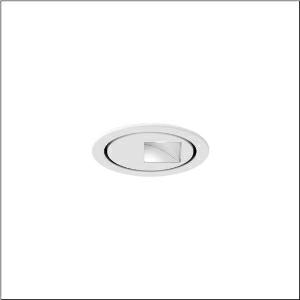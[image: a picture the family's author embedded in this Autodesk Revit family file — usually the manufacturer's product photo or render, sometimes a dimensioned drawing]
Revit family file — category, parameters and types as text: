
# Revit family: lunis_11_micro_round_51dj11b71wg21
name_source: partatom
category: Lighting Fixtures
units: mm (PartAtom-declared; Revit-internal decimal feet)

## family parameters
Cut with Voids When Loaded = No
Host = Face
Light Source = No
Part Type = Normal
Room Calculation Point = No
Round Connector Dimension = Use Diameter
Shared = No

## types (1)
- Lunis 11 micro round (1 x LED 4000K / CRI = 80 (unbekannt), 1400 lm, 4000K)
    Apparent Load = 20 VA
    CIE Flux Codes = 42 75 96 100 100
    Color Rendering = 80
    Color Temperature = 4000K
    Default Elevation = 1800 mm
    Description = Lunis 11 micro round, downlight, light control with wallwasher, of highly reflective aluminium, highly specular, light emission: direct distribution, LED rated luminous flux: 1.400lm, light colour: 840, with terminal, 3-pole, mains connection: 220..230V, AC, 50/60Hz, LED module, of aluminium, highly specular, white, diameter: 114mm, clamping range: 1..40mm, recessing ring, of plastic, traffic white (RAL 9016), protection rating (complete): IP20, insulation class (complete): insulation class II (safety insulation), certification: CE, permissible ambient temperature for indoor applications: 0..+35°C, packaging unit: 1 piece
    Height = 0 mm  [stored 0 ft]
    Lamp = 1 x LED 4000K / CRI >= 80 (unbekannt)
    Lamp Light Flux = 1400 lm
    Lamp count = 1
    Length = 114 mm
    Luminous efficacy = 71 lm/W
    Manufacturer = Siteco
    ModVariant = No
    Model = 51DJ11B71WG21
    Mounting Place = Ceiling
    Mounting Type = Recessed
    Number of Poles = 1
    OnlyDefault = Yes
    Power Factor = 1
    Product Name = Lunis 11 micro round
    Product group = downlight
    ProductGroupID = 400
    Protection Class = Protection class II
    Protection Degree = IP 20
    RLX_Detail_Level = 1
    RLX_Emergency_Light_Flux = 0 lm
    RLX_Emergency_Type = 0
    RLX_Emergency_Type_DB = No
    RlxData = <blob elided: 40845 chars, md5=f4efef6d>
    Socket = socket
    Standby Power = 0 W
    System Light Flux = 1400 lm
    System Power = 20 W
    Type Comments = Product without accessories
    Type Image = l_1004773.jpg
    URL = http://relux.com
    VarID = ---
    Voltage = 0 V
    Weight = 0.00 kg
    Width = 114 mm

note: [stored X ft] marks values corroborated as IEEE doubles in the binary element streams (Revit-internal decimal feet)

## geometry (parser evidence)
native form markers: Blend x4, Sweep x11
no freeform markers — native parametric forms only
